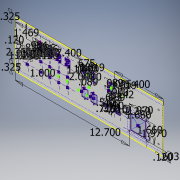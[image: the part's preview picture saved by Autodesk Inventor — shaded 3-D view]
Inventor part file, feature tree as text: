
AUTODESK INVENTOR PART (.ipt)
format: ipt  version: 2017 (Build 210142000, 142)  size: 455,168 bytes
history: native  units: in
note: dims shown in document units (in); Inventor stores cm internally (conversion verified against a paired STEP export)
features: extrude x6, other x6, hole x6, fillet x3, projected_geometry x2, sketch x1
ambient origin geometry x8: Origin, YZ Plane, XZ Plane, XY Plane, X Axis, Y Axis, Z Axis, Center Point
bodies: Solid1 (feature_tree)
feature tree (24):
  extrude  "pdu"  Depth=5.22in
  other  "dsub9 sketch"
  other  "CAT7 sketch"
  other  "airflow sketch"
  extrude  "airflow cutout"  Depth=0.065in TaperAngle=0.0deg
  extrude  "sma cutouts"  Depth=0.325in
  other  "lc and sc"
  hole  "lc hole"  [1 undecoded]
  hole  "airflow holes"  [1 undecoded]
  extrude  "Extrusion13"  Depth=1.0in
  hole  "Hole8"  [1 undecoded]
  extrude  "Extrusion14"  Depth=0.9in
  hole  "sc hole"  [1 undecoded]
  fillet  "lc fillets"  Radius=0.089in
  fillet  "sc fillets"  Radius=1.142in
  hole  "Hole13"  [1 undecoded]
  extrude  "Extrusion16"  TaperAngle=0.0deg  [1 undecoded]
  hole  "Hole14"  [1 undecoded]
  fillet  "Fillet4"  [1 undecoded]
  sketch  "Sketch1"  dims[d0=16.49in d1=5.22in d2=0.065in d3=0.0in d13=0.325in d14=0.325in d15=0.12in d16=0.12in d22=1.5748in d24=1.5in d25=0.3937in d27=1.0in d47=0.9in d49=0.089in d50=0.089in d51=1.142in d54=0.7874in d56=1.852in d57=0.3937in d59=1.0in d94=0.0in d95=0.0in d123=0.25in d124=0.235in d128=0.0in d129=0.0in d138=1.5748in d140=0.3937in d143=1.5748in d145=0.3937in d146=0.9in d147=0.675in d148=0.089in d149=0.089in d150=1.142in d152=1.019in d156=0.094in d157=0.75in d158=0.173in d159=0.25in d160=90.0deg d161=1.0in d162=0.8108in d189=0.7874in d191=1.5in d192=0.3937in d194=1.0in d196=0.7874in d198=1.0in d199=0.3937in d201=1.0in d203=1.5748in d205=1.0in d206=0.3937in d208=1.0in d221=12.7in d222=0.603in d223=1.97in d224=1.97in d225=1.66in d226=1.66in d227=0.177in d228=0.75in d229=0.119in d230=0.25in d231=0.5635in d232=1.0in d233=0.8108in d234=0.7874in d236=1.0in d237=0.7874in d239=2.0in d243=5.4in d244=7.4in d245=0.675in d246=1.019in d247=0.512in d248=0.374in d249=0.71in d253=1.0in d254=0.0in d255=0.116in d256=0.75in d257=0.119in d258=0.25in d259=0.5635in d260=1.0in d261=0.8108in d262=0.4in d263=0.71in d264=0.516in d265=0.38in d266=0.4in d267=1.0in d268=0.0in d269=0.096in d270=0.75in d271=0.172in d272=0.25in d273=0.5635in d274=1.0in d275=0.8108in d277=0.02in d278=0.02in d279=2.36in d280=0.75in d281=4.3in d282=0.46in d286=0.75in d287=4.3in d288=0.46in d291=0.5in d292=0.5in d293=0.5in d295=0.5in d297=0.236in d298=0.236in d306=0.236in d307=0.236in d322=0.169in d323=0.75in d324=0.37in d325=0.25in d326=90.0deg d327=1.0in d328=0.8108in d381=0.126in d383=1.5748in d385=0.3937in d386=0.126in d388=1.5748in d390=0.3937in d391=0.126in d393=1.5748in d395=0.3937in d396=0.126in d397=0.631in d399=0.44in d401=0.9843in d402=1.469in d403=2.85in d404=1.5748in d406=1.0in d407=0.3937in d409=1.0in d411=1.0in d412=0.0in d413=0.116in d414=0.75in d415=0.375in d416=0.25in d417=0.5635in d418=1.0in d419=0.8108in d420=0.6871in d421=0.026in d422=0.026in d423=1.35in d424=2.365in d425=0.7812in d96=1.0in d97=1.0in]
  other  "sma"
  projected_geometry  "Projected Loop1"
  projected_geometry  "Projected Loop2"
  other  "brackets"
note: 8 required parameter values undecoded (feature->parameter linkage not recoverable at this tier; creation-order binding heuristic only, values carry confidence <= 0.55)
